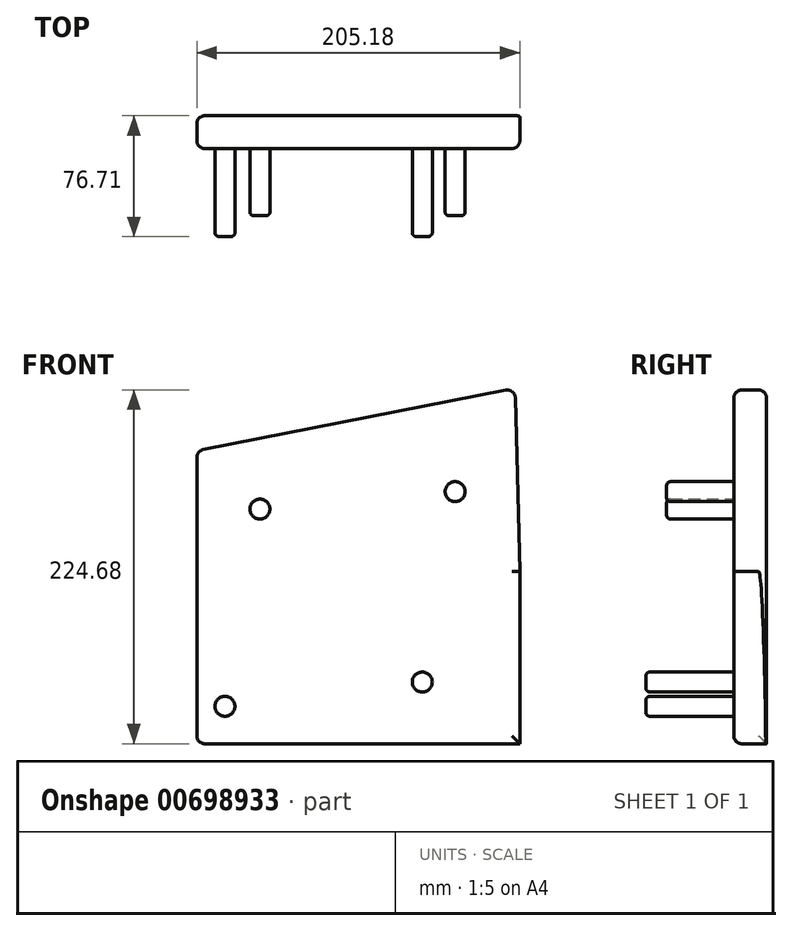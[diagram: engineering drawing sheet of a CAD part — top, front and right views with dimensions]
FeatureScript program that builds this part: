
annotation { "Feature Type Name" : "Feature", "Feature Type Description" : "" }
export const myFeature = defineFeature(function(context is Context, id is Id, definition is map)
    precondition{}
    {
        {
            var Q0;
            Q0=qCreatedBy(makeId("Front.planeOp"),FACE);
            var sketch = newSketch(context, id + "F0", { "sketchPlane" : qUnion([Q0])});
            skLineSegment(sketch, "E0", {"start": v(122.4, 65.61) * mm, "end": v(-79.75, 25.91) * mm});
            skLineSegment(sketch, "E1", {"start": v(-79.75, 25.91) * mm, "end": v(-79.75, -47.73) * mm});
            skLineSegment(sketch, "E2", {"start": v(-79.75, -47.73) * mm, "end": v(125.43, -50.76) * mm});
            skLineSegment(sketch, "E3", {"start": v(125.43, -50.76) * mm, "end": v(122.4, 65.61) * mm});
            skLineSegment(sketch, "E4", {"start": v(-79.75, -47.73) * mm, "end": v(-79.75, -160.13) * mm});
            skLineSegment(sketch, "E5", {"start": v(-79.75, -160.13) * mm, "end": v(125.43, -160.13) * mm});
            skLineSegment(sketch, "E6", {"start": v(125.43, -160.13) * mm, "end": v(125.43, -50.76) * mm});
            skSolve(sketch);
        }
        {
            var Q0;
            Q0 = qSketchRegion(id + "F0", true);
            extrude(context, id + "F1", {"entities" : qUnion([Q0]), "depth" : 20.83 * mm, "offsetDistance" : 25.4 * mm});
        }
        {
            var Q0;
            Q0=makeQuery(id+"F1.opExtrude","CAP_EDGE",EDGE,{"disambiguationData":[OSD([sQuery(id+"F0.wireOp",EDGE,"E0")])],"isStart":true});
            var Q1;
            Q1=makeQuery(id+"F1.opExtrude","CAP_FACE",FACE,{"disambiguationData":[OSD([sQuery(id+"F0.wireOp",EDGE,"E0"),sQuery(id+"F0.wireOp",EDGE,"E1"),sQuery(id+"F0.wireOp",EDGE,"E2"),sQuery(id+"F0.wireOp",EDGE,"E3")])],"isStart":false});
            var Q2;
            Q2=makeQuery(id+"F1.opExtrude","SWEPT_FACE",FACE,{"disambiguationData":[OSD([sQuery(id+"F0.wireOp",EDGE,"E1")])]});
            var Q3;
            Q3=makeQuery(id+"F1.opExtrude","SWEPT_FACE",FACE,{"disambiguationData":[OSD([sQuery(id+"F0.wireOp",EDGE,"E0")])]});
            var Q4;
            Q4=makeQuery(id+"F1.opExtrude","SWEPT_FACE",FACE,{"disambiguationData":[OSD([sQuery(id+"F0.wireOp",EDGE,"E2")])]});
            var Q5;
            Q5=makeQuery(id+"F1.opExtrude","CAP_EDGE",EDGE,{"disambiguationData":[OSD([sQuery(id+"F0.wireOp",EDGE,"E3")])],"isStart":true});
            fillet(context, id + "F2", {"entities" : qUnion([Q0, Q1, Q2, Q3, Q4, Q5]), "radius" : 5.08 * mm, "tangentPropagation" : true, "allowEdgeOverflow" : false});
        }
        {
            var Q0;
            Q0=makeQuery(id+"F1.opExtrude","CAP_FACE",FACE,{"disambiguationData":[OSD([sQuery(id+"F0.wireOp",EDGE,"E0"),sQuery(id+"F0.wireOp",EDGE,"E1"),sQuery(id+"F0.wireOp",EDGE,"E2"),sQuery(id+"F0.wireOp",EDGE,"E3")])],"isStart":false});
            var sketch = newSketch(context, id + "F3", { "sketchPlane" : qUnion([Q0])});
            skCircle(sketch, "E7", {"center": v(-39.66, -11.06) * mm, "radius": 6.35 * mm});
            skCircle(sketch, "E8", {"center": v(84.3, 0) * mm, "radius": 6.35 * mm});
            skSolve(sketch);
        }
        {
            var Q0;
            Q0 = qSketchRegion(id + "F3", true);
            extrude(context, id + "F4", {"entities" : qUnion([Q0]), "operationType" : NewBodyOperationType.ADD, "depth" : 42.67 * mm, "offsetDistance" : 25.4 * mm});
        }
        {
            var Q0;
            Q0=makeQuery(id+"F4.opExtrude","CAP_EDGE",EDGE,{"disambiguationData":[OSD([sQuery(id+"F3.wireOp",EDGE,"E8")])],"isStart":false});
            var Q1;
            Q1=makeQuery(id+"F4.opExtrude","CAP_EDGE",EDGE,{"disambiguationData":[OSD([sQuery(id+"F3.wireOp",EDGE,"E7")])],"isStart":false});
            fillet(context, id + "F5", {"entities" : qUnion([Q0, Q1]), "radius" : 2.45 * mm, "tangentPropagation" : true, "allowEdgeOverflow" : false});
        }
        {
            var Q0;
            Q0=makeQuery(id+"F1.opExtrude","CAP_FACE",FACE,{"disambiguationData":[OSD([sQuery(id+"F0.wireOp",EDGE,"E0"),sQuery(id+"F0.wireOp",EDGE,"E1"),sQuery(id+"F0.wireOp",EDGE,"E3"),sQuery(id+"F0.wireOp",EDGE,"E4"),sQuery(id+"F0.wireOp",EDGE,"E5"),sQuery(id+"F0.wireOp",EDGE,"E6")])],"isStart":false});
            var sketch = newSketch(context, id + "F6", { "sketchPlane" : qUnion([Q0])});
            skCircle(sketch, "E9", {"center": v(-61.86, -136.37) * mm, "radius": 6.35 * mm});
            skCircle(sketch, "E10", {"center": v(63.44, -120.9) * mm, "radius": 6.35 * mm});
            skSolve(sketch);
        }
        {
            var Q0;
            Q0 = qSketchRegion(id + "F6", true);
            extrude(context, id + "F7", {"entities" : qUnion([Q0]), "operationType" : NewBodyOperationType.ADD, "depth" : 55.88 * mm, "offsetDistance" : 25.4 * mm});
        }
        {
            var Q0;
            Q0=makeQuery(id+"F7.opExtrude","CAP_EDGE",EDGE,{"disambiguationData":[OSD([sQuery(id+"F6.wireOp",EDGE,"E10")])],"isStart":false});
            var Q1;
            Q1=makeQuery(id+"F7.opExtrude","CAP_EDGE",EDGE,{"disambiguationData":[OSD([sQuery(id+"F6.wireOp",EDGE,"E9")])],"isStart":false});
            fillet(context, id + "F8", {"entities" : qUnion([Q0, Q1]), "radius" : 2.54 * mm, "tangentPropagation" : true, "allowEdgeOverflow" : false});
        }
    });
